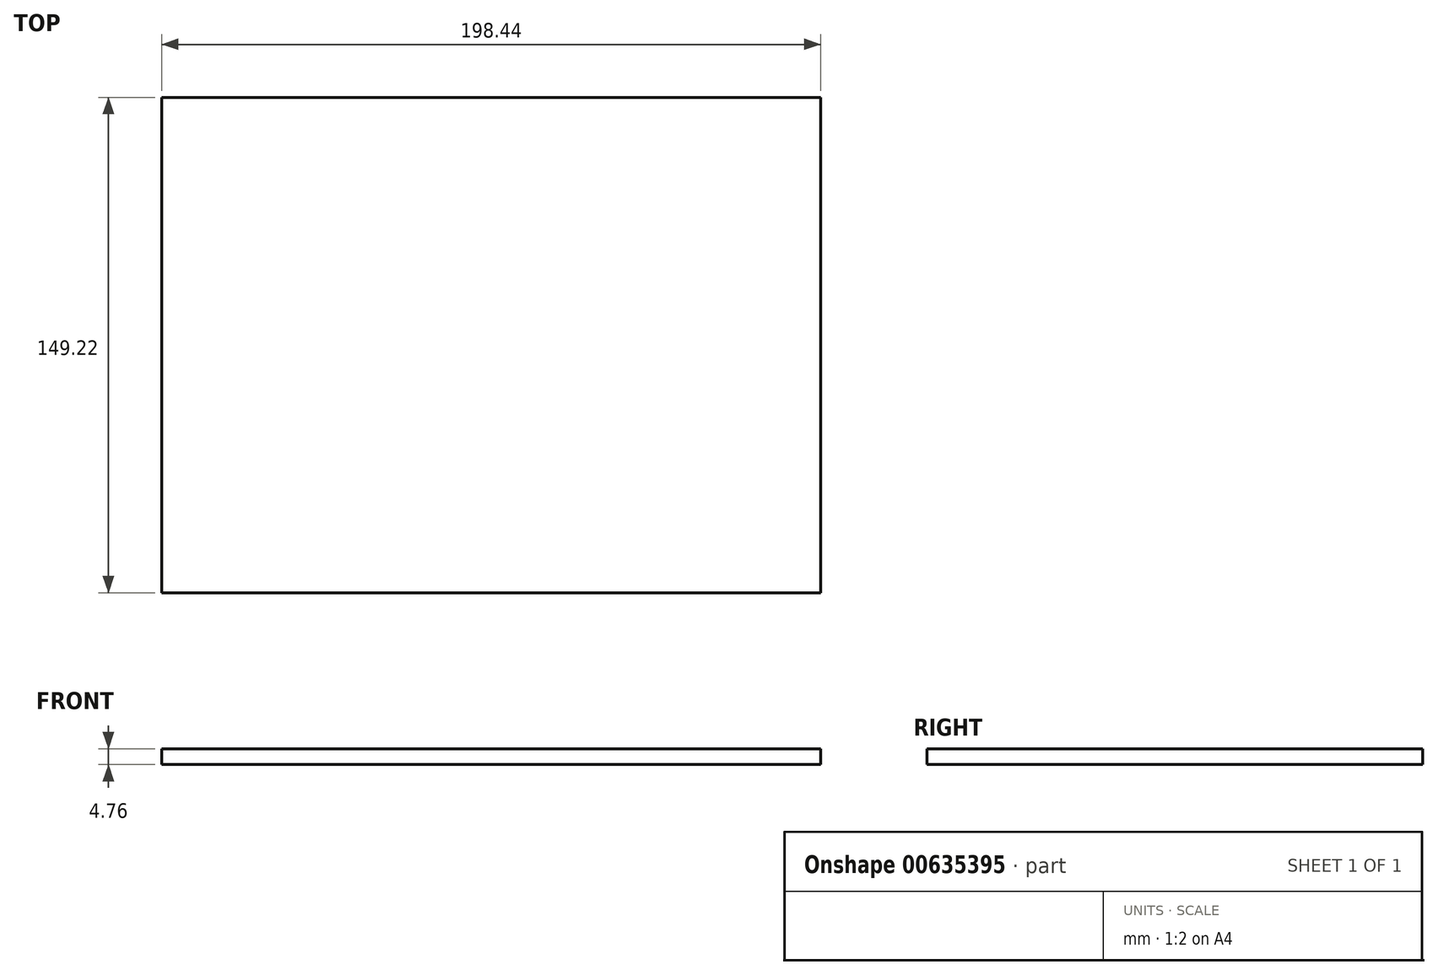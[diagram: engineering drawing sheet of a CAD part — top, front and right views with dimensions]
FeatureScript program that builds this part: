
annotation { "Feature Type Name" : "Feature", "Feature Type Description" : "" }
export const myFeature = defineFeature(function(context is Context, id is Id, definition is map)
    precondition{}
    {
        {
            var Q0;
            Q0=qCreatedBy(makeId("Top.planeOp"),FACE);
            var sketch = newSketch(context, id + "F0", { "sketchPlane" : qUnion([Q0])});
            skLineSegment(sketch, "E0.bottom", {"start": v(-99.22, 74.61) * mm, "end": v(99.22, 74.61) * mm});
            skLineSegment(sketch, "E0.top", {"start": v(-99.22, -74.61) * mm, "end": v(99.22, -74.61) * mm});
            skLineSegment(sketch, "E0.left", {"start": v(-99.22, 74.61) * mm, "end": v(-99.22, -74.61) * mm});
            skLineSegment(sketch, "E0.right", {"start": v(99.22, 74.61) * mm, "end": v(99.22, -74.61) * mm});
            skPoint(sketch, "E0.middle", {"position": v(0, 0) * mm});
            skSolve(sketch);
        }
        {
            var Q0;
            Q0=qSketchRegion(id+"F0",true);
            extrude(context, id + "F1", {"entities" : qUnion([Q0]), "depth" : 4.76 * mm});
        }
    });
